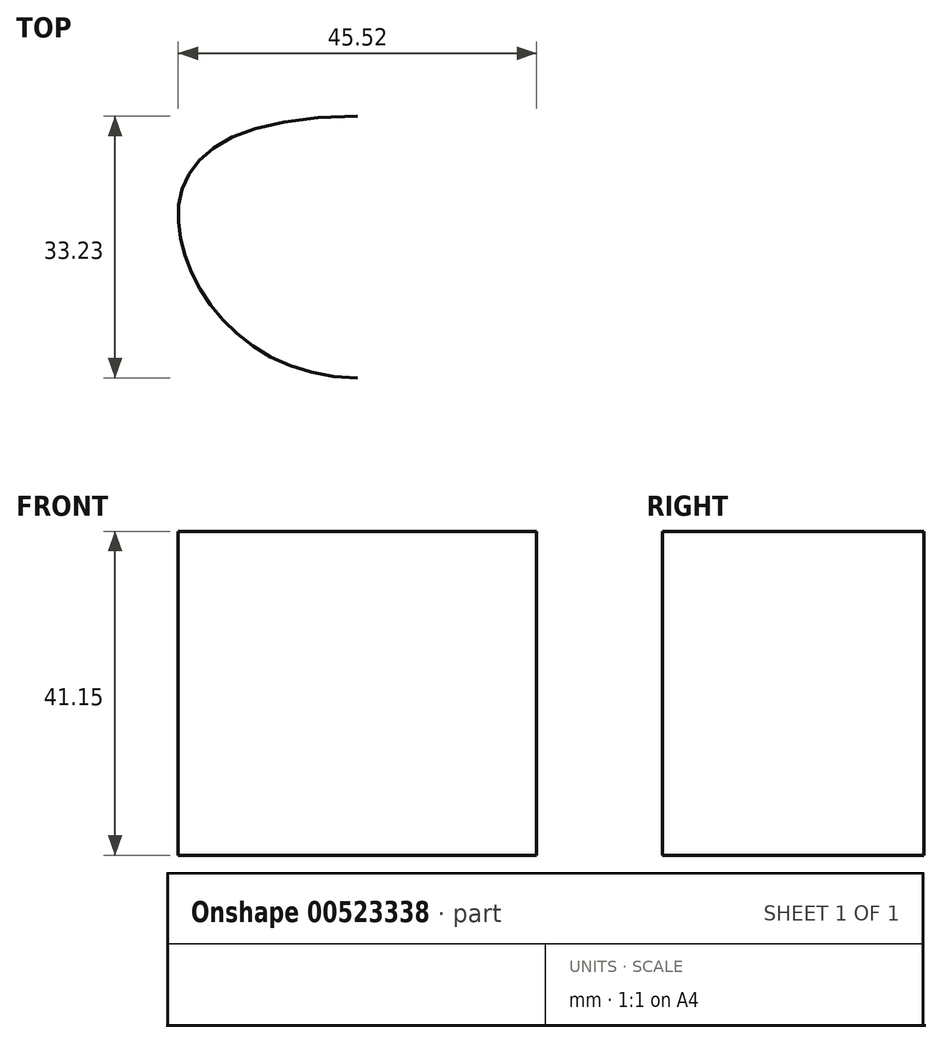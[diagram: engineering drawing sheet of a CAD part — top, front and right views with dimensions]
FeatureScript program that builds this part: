
annotation { "Feature Type Name" : "Feature", "Feature Type Description" : "" }
export const myFeature = defineFeature(function(context is Context, id is Id, definition is map)
    precondition{}
    {
        {
            var Q0;
            Q0=qCreatedBy(makeId("Top.planeOp"),FACE);
            var sketch = newSketch(context, id + "F0", { "sketchPlane" : qUnion([Q0])});
            skFitSpline(sketch, "E0", {"points": [v(0, 0) * mm, v(22.21, 16.61) * mm, v(0, 33.23) * mm], "startDerivative": vector(71.88, 0) * mm, "endDerivative": vector(-124.02, 0) * mm});
            skLineSegment(sketch, "E1", {"start": v(0, 0) * mm, "end": v(0, 33.23) * mm, "construction": true});
            skFitSpline(sketch, "E2.MirrorCS", {"points": [v(0, 0) * mm, v(-22.21, 16.61) * mm, v(0, 33.23) * mm], "startDerivative": vector(-71.88, 0) * mm, "endDerivative": vector(124.02, 0) * mm});
            skPoint(sketch, "E3", {"position": v(0, 16.61) * mm});
            skSolve(sketch);
        }
        {
            var Q0;
            Q0 = qSketchRegion(id + "F0", true);
            extrude(context, id + "F1", {"entities" : qUnion([Q0]), "depth" : 41.15 * mm, "offsetDistance" : 25.4 * mm});
        }
    });
